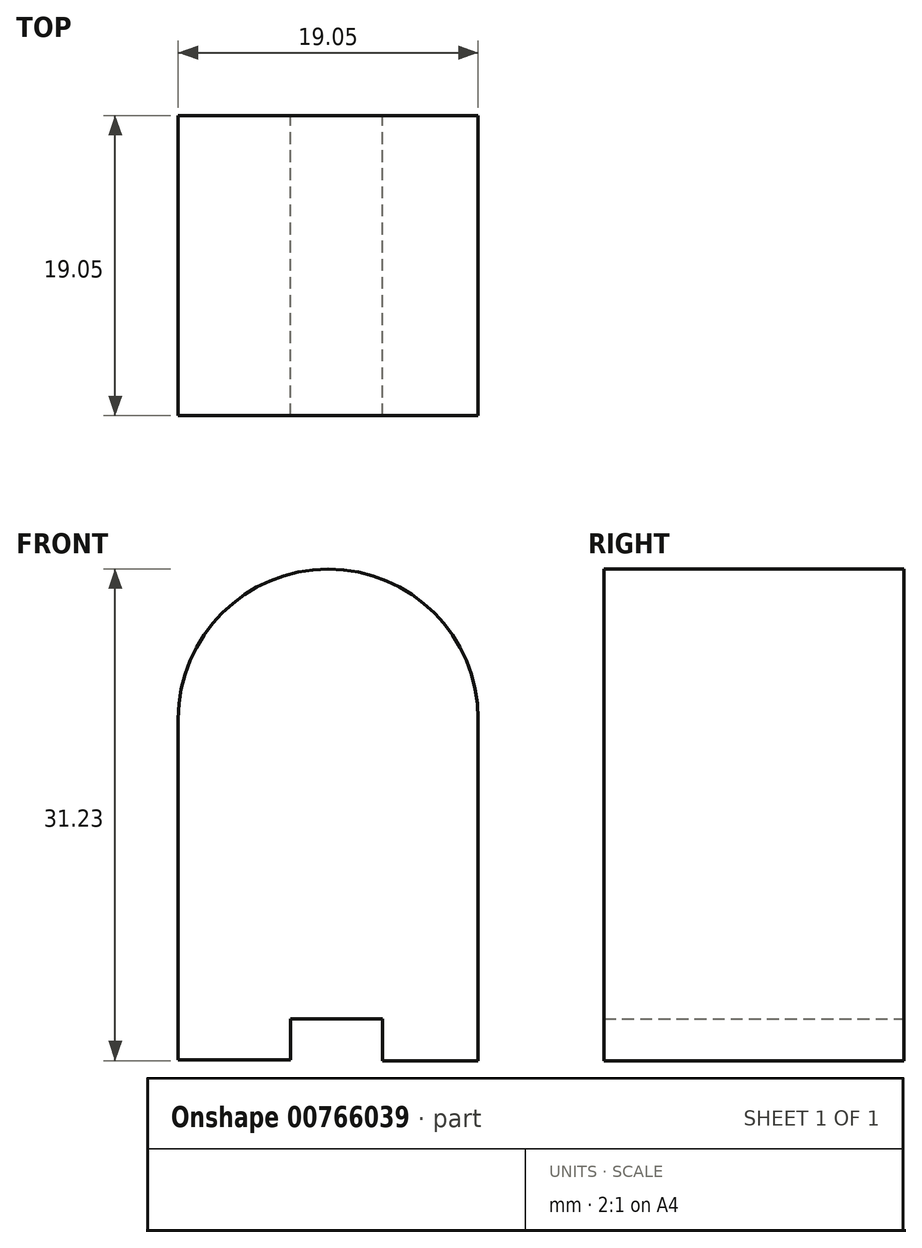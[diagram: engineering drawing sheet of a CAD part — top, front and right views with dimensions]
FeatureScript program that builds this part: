
annotation { "Feature Type Name" : "Feature", "Feature Type Description" : "" }
export const myFeature = defineFeature(function(context is Context, id is Id, definition is map)
    precondition{}
    {
        {
            var Q0;
            Q0=qCreatedBy(makeId("Front.planeOp"),FACE);
            var sketch = newSketch(context, id + "F0", { "sketchPlane" : qUnion([Q0])});
            skArc(sketch, "E0", {"start": v(9.68, 0) * mm, "mid": v(0.16, 9.52) * mm, "end": v(-9.37, 0) * mm});
            skLineSegment(sketch, "E1", {"start": v(-9.37, 0) * mm, "end": v(9.68, 0) * mm});
            skLineSegment(sketch, "E2", {"start": v(-9.37, 0) * mm, "end": v(-9.37, -19.05) * mm});
            skLineSegment(sketch, "E3", {"start": v(-9.37, -19.05) * mm, "end": v(9.68, -19.05) * mm});
            skLineSegment(sketch, "E4", {"start": v(9.68, -19.05) * mm, "end": v(9.68, 0) * mm});
            skLineSegment(sketch, "E5", {"start": v(0.16, 9.53) * mm, "end": v(0.16, -19.05) * mm});
            skLineSegment(sketch, "E6", {"start": v(-9.37, -19.05) * mm, "end": v(-9.37, -21.64) * mm});
            skLineSegment(sketch, "E7", {"start": v(-9.37, -21.64) * mm, "end": v(-2.23, -21.64) * mm});
            skLineSegment(sketch, "E8", {"start": v(-2.23, -21.64) * mm, "end": v(-2.23, -19.05) * mm});
            skLineSegment(sketch, "E9", {"start": v(9.68, -19.05) * mm, "end": v(9.68, -21.7) * mm});
            skLineSegment(sketch, "E10", {"start": v(9.68, -21.7) * mm, "end": v(3.6, -21.7) * mm});
            skLineSegment(sketch, "E11", {"start": v(3.6, -21.7) * mm, "end": v(3.6, -19.05) * mm});
            skSolve(sketch);
        }
        {
            var Q0;
            {var subQ0=sQuery(id+"F0.wireOp",EDGE,"E6");Q0=makeQuery(id+"F0.imprint","IMPRINT",FACE,{"disambiguationData":[TD([[makeQuery(id+"F0.imprint","IMPRINT",EDGE,{"derivedFrom":subQ0}),1.0]])]});}
            var Q1;
            {var subQ4=sQuery(id+"F0.wireOp",EDGE,"E2");Q1=makeQuery(id+"F0.imprint","IMPRINT",FACE,{"disambiguationData":[TD([[makeQuery(id+"F0.imprint","IMPRINT",EDGE,{"derivedFrom":subQ4}),1.0]])]});}
            var Q2;
            {var subQ1=sQuery(id+"F0.wireOp",EDGE,"E0");var subQ3=sQuery(id+"F0.wireOp",EDGE,"E5");var subQ4=makeQuery(id+"F0.imprint","INTERSECT",VERTEX,{"derivedFrom":[subQ1,subQ3]});Q2=makeQuery(id+"F0.imprint","IMPRINT",FACE,{"disambiguationData":[TD([[makeQuery(id+"F0.imprint","IMPRINT",EDGE,{"disambiguationData":[TD([[subQ4,-1.0]])],"derivedFrom":subQ3}),-1.0]])]});}
            var Q3;
            {var subQ1=sQuery(id+"F0.wireOp",EDGE,"E0");var subQ3=sQuery(id+"F0.wireOp",EDGE,"E5");var subQ4=makeQuery(id+"F0.imprint","INTERSECT",VERTEX,{"derivedFrom":[subQ1,subQ3]});Q3=makeQuery(id+"F0.imprint","IMPRINT",FACE,{"disambiguationData":[TD([[makeQuery(id+"F0.imprint","IMPRINT",EDGE,{"disambiguationData":[TD([[subQ4,-1.0]])],"derivedFrom":subQ3}),1.0]])]});}
            var Q4;
            {var subQ0=sQuery(id+"F0.wireOp",EDGE,"E4");Q4=makeQuery(id+"F0.imprint","IMPRINT",FACE,{"disambiguationData":[TD([[makeQuery(id+"F0.imprint","IMPRINT",EDGE,{"derivedFrom":subQ0}),1.0]])]});}
            var Q5;
            {var subQ0=sQuery(id+"F0.wireOp",EDGE,"E9");Q5=makeQuery(id+"F0.imprint","IMPRINT",FACE,{"disambiguationData":[TD([[makeQuery(id+"F0.imprint","IMPRINT",EDGE,{"derivedFrom":subQ0}),-1.0]])]});}
            extrude(context, id + "F1", {"entities" : qUnion([Q0, Q1, Q2, Q3, Q4, Q5]), "depth" : 19.05 * mm, "offsetDistance" : 25.4 * mm});
        }
    });
